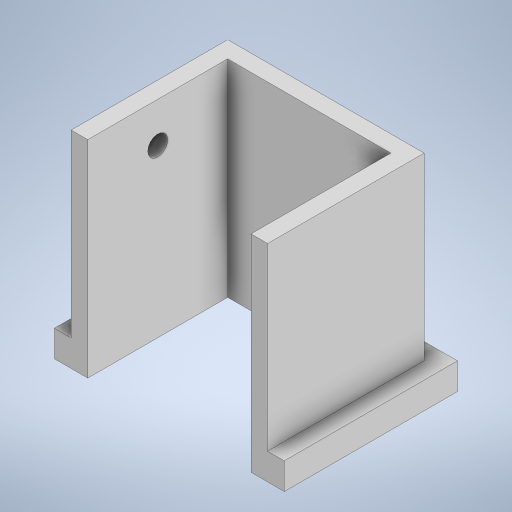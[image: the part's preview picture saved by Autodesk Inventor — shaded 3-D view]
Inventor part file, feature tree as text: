
AUTODESK INVENTOR PART (.ipt)
format: ipt  version: 2023 (Build 270158000, 158)  size: 262,144 bytes
history: native  units: in
note: dims shown in document units (in); Inventor stores cm internally (conversion verified against a paired STEP export)
features: sketch x5, extrude x4
ambient origin geometry x8: Origin, YZ Plane, XZ Plane, XY Plane, X Axis, Y Axis, Z Axis, Center Point
bodies: Solid1 (feature_tree)
feature tree (9):
  extrude  "Extrusion1"  Depth=0.1969in
  extrude  "Extrusion7"  Depth=1.6535in
  extrude  "Extrusion8"  Depth=1.6535in
  sketch  "Sketch9"  dims[d6=2.4409in d7=0.0in d34=0.1969in]
  extrude  "Extrusion9"  Depth=0.1969in
  sketch  "Sketch1"  dims[d0=2.3228in d1=0.1969in]
  sketch  "Sketch7"  dims[d2=0.1969in d3=1.6535in]
  sketch  "Sketch8"  dims[d4=0.1969in d5=1.6535in]
  sketch  "Sketch10"  dims[d35=2.0472in d36=0.1969in d37=2.0472in d38=0.315in d39=0.0in d40=0.3937in d41=0.2047in d42=0.3937in d43=0.2047in d44=1.3583in d47=0.2047in d48=0.2047in d49=0.1969in d50=0.0in d51=0.8268in d52=1.9685in d53=0.2362in d54=0.1969in d55=0.0in d56=0.5118in d57=0.5118in d11=0.0197in d12=0.0344in d13=0.0197in d14=0.0344in]
